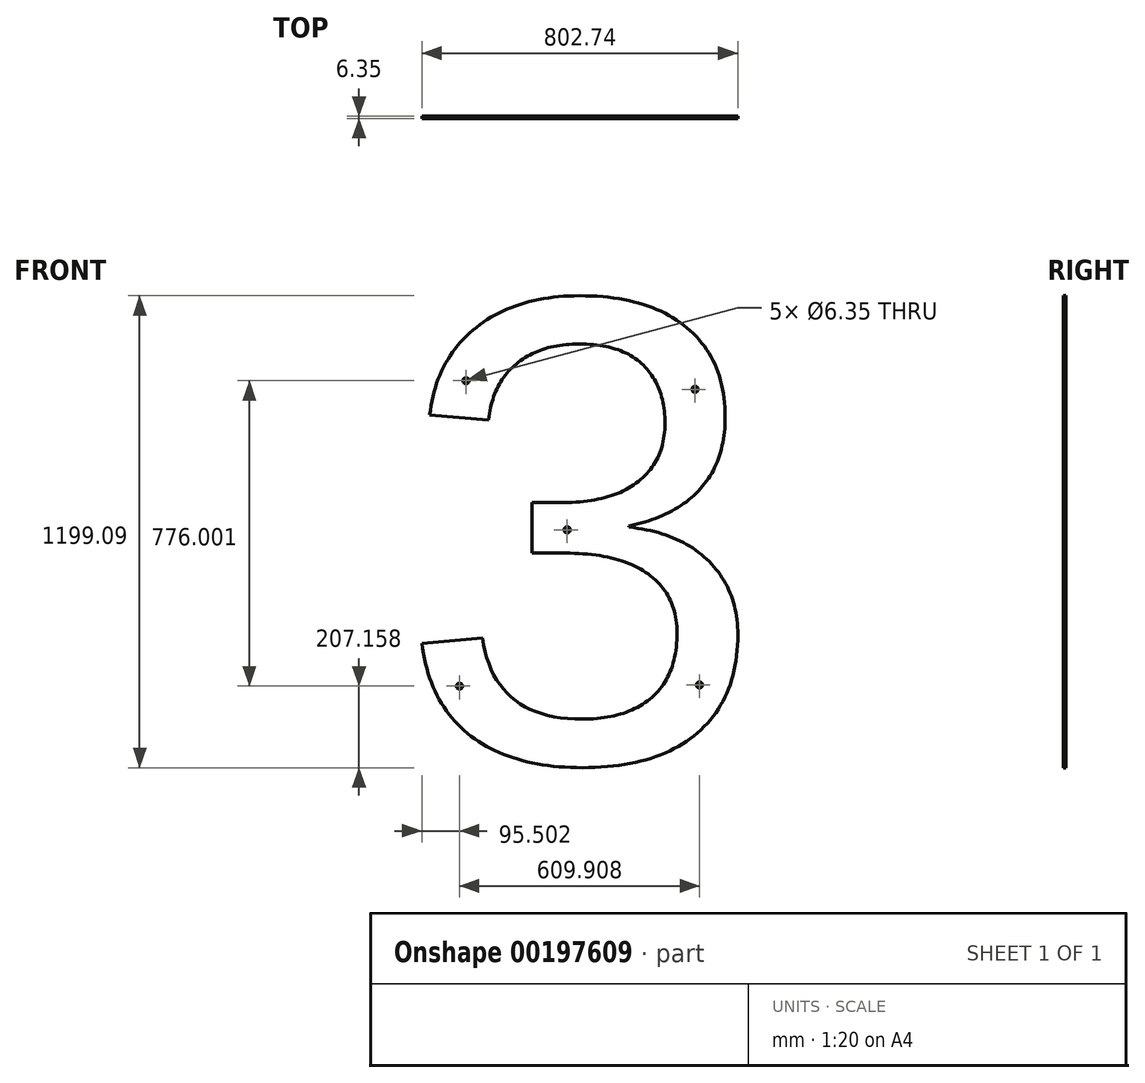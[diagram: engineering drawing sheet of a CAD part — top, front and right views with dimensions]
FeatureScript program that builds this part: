
annotation { "Feature Type Name" : "Feature", "Feature Type Description" : "" }
export const myFeature = defineFeature(function(context is Context, id is Id, definition is map)
    precondition{}
    {
        {
            var Q0;
            Q0=qCreatedBy(makeId("Front.planeOp"),FACE);
            var sketch = newSketch(context, id + "F0", { "sketchPlane" : qUnion([Q0])});
            skText(sketch, "E0", { "text": "3", "fontName": "Arimo-Regular.ttf"});
            const initialGuessF0  = {"E0": [-0.12572, -0.58621, 1, 0, 1.2192]};
            skSetInitialGuess(sketch, initialGuessF0);
            skSolve(sketch);
        }
        {
            var Q0;
            Q0=makeQuery(id+"F0.imprint","IMPRINT",FACE,{"disambiguationData":[TD([[makeQuery(id+"F0.imprint","IMPRINT",EDGE,{"derivedFrom":sQuery(id+"F0.wireOp",EDGE,"E0.sketch_text.stroke-0")}),-1.0]])]});
            extrude(context, id + "F1", {"entities" : qUnion([Q0]), "depth" : 6.35 * mm});
        }
        {
            var Q0;
            Q0=makeQuery(id+"F1.opExtrude","CAP_FACE",FACE,{"disambiguationData":[OSD([sQuery(id+"F0.wireOp",EDGE,"E0.sketch_text.stroke-0"),sQuery(id+"F0.wireOp",EDGE,"E0.sketch_text.stroke-1"),sQuery(id+"F0.wireOp",EDGE,"E0.sketch_text.stroke-2"),sQuery(id+"F0.wireOp",EDGE,"E0.sketch_text.stroke-3"),sQuery(id+"F0.wireOp",EDGE,"E0.sketch_text.stroke-4"),sQuery(id+"F0.wireOp",EDGE,"E0.sketch_text.stroke-5"),sQuery(id+"F0.wireOp",EDGE,"E0.sketch_text.stroke-6"),sQuery(id+"F0.wireOp",EDGE,"E0.sketch_text.stroke-7"),sQuery(id+"F0.wireOp",EDGE,"E0.sketch_text.stroke-8"),sQuery(id+"F0.wireOp",EDGE,"E0.sketch_text.stroke-9"),sQuery(id+"F0.wireOp",EDGE,"E0.sketch_text.stroke-10"),sQuery(id+"F0.wireOp",EDGE,"E0.sketch_text.stroke-11"),sQuery(id+"F0.wireOp",EDGE,"E0.sketch_text.stroke-12"),sQuery(id+"F0.wireOp",EDGE,"E0.sketch_text.stroke-13"),sQuery(id+"F0.wireOp",EDGE,"E0.sketch_text.stroke-14"),sQuery(id+"F0.wireOp",EDGE,"E0.sketch_text.stroke-15"),sQuery(id+"F0.wireOp",EDGE,"E0.sketch_text.stroke-16"),sQuery(id+"F0.wireOp",EDGE,"E0.sketch_text.stroke-17"),sQuery(id+"F0.wireOp",EDGE,"E0.sketch_text.stroke-18"),sQuery(id+"F0.wireOp",EDGE,"E0.sketch_text.stroke-19"),sQuery(id+"F0.wireOp",EDGE,"E0.sketch_text.stroke-20"),sQuery(id+"F0.wireOp",EDGE,"E0.sketch_text.stroke-21"),sQuery(id+"F0.wireOp",EDGE,"E0.sketch_text.stroke-22"),sQuery(id+"F0.wireOp",EDGE,"E0.sketch_text.stroke-23"),sQuery(id+"F0.wireOp",EDGE,"E0.sketch_text.stroke-24"),sQuery(id+"F0.wireOp",EDGE,"E0.sketch_text.stroke-25"),sQuery(id+"F0.wireOp",EDGE,"E0.sketch_text.stroke-26"),sQuery(id+"F0.wireOp",EDGE,"E0.sketch_text.stroke-27"),sQuery(id+"F0.wireOp",EDGE,"E0.sketch_text.stroke-28")])],"isStart":false});
            var sketch = newSketch(context, id + "F2", { "sketchPlane" : qUnion([Q0])});
            skCircle(sketch, "E1", {"center": v(50.97, 380.28) * mm, "radius": 7.75 * mm});
            skCircle(sketch, "E2", {"center": v(632.87, 358.46) * mm, "radius": 7.75 * mm});
            skCircle(sketch, "E3", {"center": v(308.03, 1.41) * mm, "radius": 7.75 * mm});
            skCircle(sketch, "E4", {"center": v(644.25, -392.7) * mm, "radius": 7.75 * mm});
            skCircle(sketch, "E5", {"center": v(34.34, -395.72) * mm, "radius": 7.75 * mm});
            skSolve(sketch);
        }
        {
            var Q0;
            Q0=sQuery(id+"F2.wireOp",VERTEX,"7F1VabAT-elt8-ZJh5-0tXk-MR5qx3RPOEMj.center");
            var Q1;
            Q1=sQuery(id+"F2.wireOp",VERTEX,"E4.center");
            var Q2;
            Q2=sQuery(id+"F2.wireOp",VERTEX,"E3.center");
            var Q3;
            Q3=sQuery(id+"F2.wireOp",VERTEX,"E2.center");
            var Q4;
            Q4=sQuery(id+"F2.wireOp",VERTEX,"E1.center");
            var Q5;
            Q5=makeQuery(id+"F1.opExtrude","SWEPT_BODY",BODY,{"disambiguationData":[OSD([sQuery(id+"F0.wireOp",EDGE,"E0.sketch_text.stroke-0"),sQuery(id+"F0.wireOp",EDGE,"E0.sketch_text.stroke-1"),sQuery(id+"F0.wireOp",EDGE,"E0.sketch_text.stroke-2"),sQuery(id+"F0.wireOp",EDGE,"E0.sketch_text.stroke-3"),sQuery(id+"F0.wireOp",EDGE,"E0.sketch_text.stroke-4"),sQuery(id+"F0.wireOp",EDGE,"E0.sketch_text.stroke-5"),sQuery(id+"F0.wireOp",EDGE,"E0.sketch_text.stroke-6"),sQuery(id+"F0.wireOp",EDGE,"E0.sketch_text.stroke-7"),sQuery(id+"F0.wireOp",EDGE,"E0.sketch_text.stroke-8"),sQuery(id+"F0.wireOp",EDGE,"E0.sketch_text.stroke-9"),sQuery(id+"F0.wireOp",EDGE,"E0.sketch_text.stroke-10"),sQuery(id+"F0.wireOp",EDGE,"E0.sketch_text.stroke-11"),sQuery(id+"F0.wireOp",EDGE,"E0.sketch_text.stroke-12"),sQuery(id+"F0.wireOp",EDGE,"E0.sketch_text.stroke-13"),sQuery(id+"F0.wireOp",EDGE,"E0.sketch_text.stroke-14"),sQuery(id+"F0.wireOp",EDGE,"E0.sketch_text.stroke-15"),sQuery(id+"F0.wireOp",EDGE,"E0.sketch_text.stroke-16"),sQuery(id+"F0.wireOp",EDGE,"E0.sketch_text.stroke-17"),sQuery(id+"F0.wireOp",EDGE,"E0.sketch_text.stroke-18"),sQuery(id+"F0.wireOp",EDGE,"E0.sketch_text.stroke-19"),sQuery(id+"F0.wireOp",EDGE,"E0.sketch_text.stroke-20"),sQuery(id+"F0.wireOp",EDGE,"E0.sketch_text.stroke-21"),sQuery(id+"F0.wireOp",EDGE,"E0.sketch_text.stroke-22"),sQuery(id+"F0.wireOp",EDGE,"E0.sketch_text.stroke-23"),sQuery(id+"F0.wireOp",EDGE,"E0.sketch_text.stroke-24"),sQuery(id+"F0.wireOp",EDGE,"E0.sketch_text.stroke-25"),sQuery(id+"F0.wireOp",EDGE,"E0.sketch_text.stroke-26"),sQuery(id+"F0.wireOp",EDGE,"E0.sketch_text.stroke-27"),sQuery(id+"F0.wireOp",EDGE,"E0.sketch_text.stroke-28")])]});
            hole(context, id + "F3", {"style" : HoleStyle.C_SINK, "endStyle" : HoleEndStyle.THROUGH, "holeDiameter" : 6.35 * mm, "cSinkDiameter" : 15.5 * mm, "cSinkAngle" : 90 * degree, "locations" : qUnion([Q0, Q1, Q2, Q3, Q4]), "scope" : qUnion([Q5]), "isTappedThrough" : true});
        }
        {
            var Q0;
            Q0=sQuery(id+"F2.wireOp",VERTEX,"E5.center");
            var Q1;
            Q1=makeQuery(id+"F1.opExtrude","SWEPT_BODY",BODY,{"disambiguationData":[OSD([sQuery(id+"F0.wireOp",EDGE,"E0.sketch_text.stroke-0"),sQuery(id+"F0.wireOp",EDGE,"E0.sketch_text.stroke-1"),sQuery(id+"F0.wireOp",EDGE,"E0.sketch_text.stroke-2"),sQuery(id+"F0.wireOp",EDGE,"E0.sketch_text.stroke-3"),sQuery(id+"F0.wireOp",EDGE,"E0.sketch_text.stroke-4"),sQuery(id+"F0.wireOp",EDGE,"E0.sketch_text.stroke-5"),sQuery(id+"F0.wireOp",EDGE,"E0.sketch_text.stroke-6"),sQuery(id+"F0.wireOp",EDGE,"E0.sketch_text.stroke-7"),sQuery(id+"F0.wireOp",EDGE,"E0.sketch_text.stroke-8"),sQuery(id+"F0.wireOp",EDGE,"E0.sketch_text.stroke-9"),sQuery(id+"F0.wireOp",EDGE,"E0.sketch_text.stroke-10"),sQuery(id+"F0.wireOp",EDGE,"E0.sketch_text.stroke-11"),sQuery(id+"F0.wireOp",EDGE,"E0.sketch_text.stroke-12"),sQuery(id+"F0.wireOp",EDGE,"E0.sketch_text.stroke-13"),sQuery(id+"F0.wireOp",EDGE,"E0.sketch_text.stroke-14"),sQuery(id+"F0.wireOp",EDGE,"E0.sketch_text.stroke-15"),sQuery(id+"F0.wireOp",EDGE,"E0.sketch_text.stroke-16"),sQuery(id+"F0.wireOp",EDGE,"E0.sketch_text.stroke-17"),sQuery(id+"F0.wireOp",EDGE,"E0.sketch_text.stroke-18"),sQuery(id+"F0.wireOp",EDGE,"E0.sketch_text.stroke-19"),sQuery(id+"F0.wireOp",EDGE,"E0.sketch_text.stroke-20"),sQuery(id+"F0.wireOp",EDGE,"E0.sketch_text.stroke-21"),sQuery(id+"F0.wireOp",EDGE,"E0.sketch_text.stroke-22"),sQuery(id+"F0.wireOp",EDGE,"E0.sketch_text.stroke-23"),sQuery(id+"F0.wireOp",EDGE,"E0.sketch_text.stroke-24"),sQuery(id+"F0.wireOp",EDGE,"E0.sketch_text.stroke-25"),sQuery(id+"F0.wireOp",EDGE,"E0.sketch_text.stroke-26"),sQuery(id+"F0.wireOp",EDGE,"E0.sketch_text.stroke-27"),sQuery(id+"F0.wireOp",EDGE,"E0.sketch_text.stroke-28")])]});
            hole(context, id + "F4", {"style" : HoleStyle.C_SINK, "endStyle" : HoleEndStyle.THROUGH, "holeDiameter" : 6.35 * mm, "cSinkDiameter" : 15.5 * mm, "cSinkAngle" : 90 * degree, "locations" : qUnion([Q0]), "scope" : qUnion([Q1]), "isTappedThrough" : true});
        }
    });
